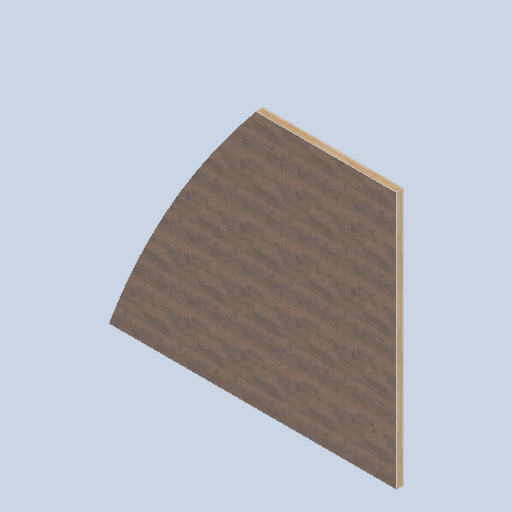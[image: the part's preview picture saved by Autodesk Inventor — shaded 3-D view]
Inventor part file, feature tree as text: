
AUTODESK INVENTOR PART (.ipt)
format: ipt  version: 2024.2 (Build 282272000, 272)  size: 190,464 bytes
history: native  units: in
note: dims shown in document units (in); Inventor stores cm internally (conversion verified against a paired STEP export)
features: other x3, sketch x1
ambient origin geometry x8: Origin, YZ Plane, XZ Plane, XY Plane, X Axis, Y Axis, Z Axis, Center Point
bodies: Solid1 (feature_tree)
feature tree (4):
  other  "front_wall_block02.ipt"
  other  "Solid1::front_wall_block02.ipt"
  other  "TaggingFeature1"
  sketch  "Sketch1"  dims[d0=0.3937in]
